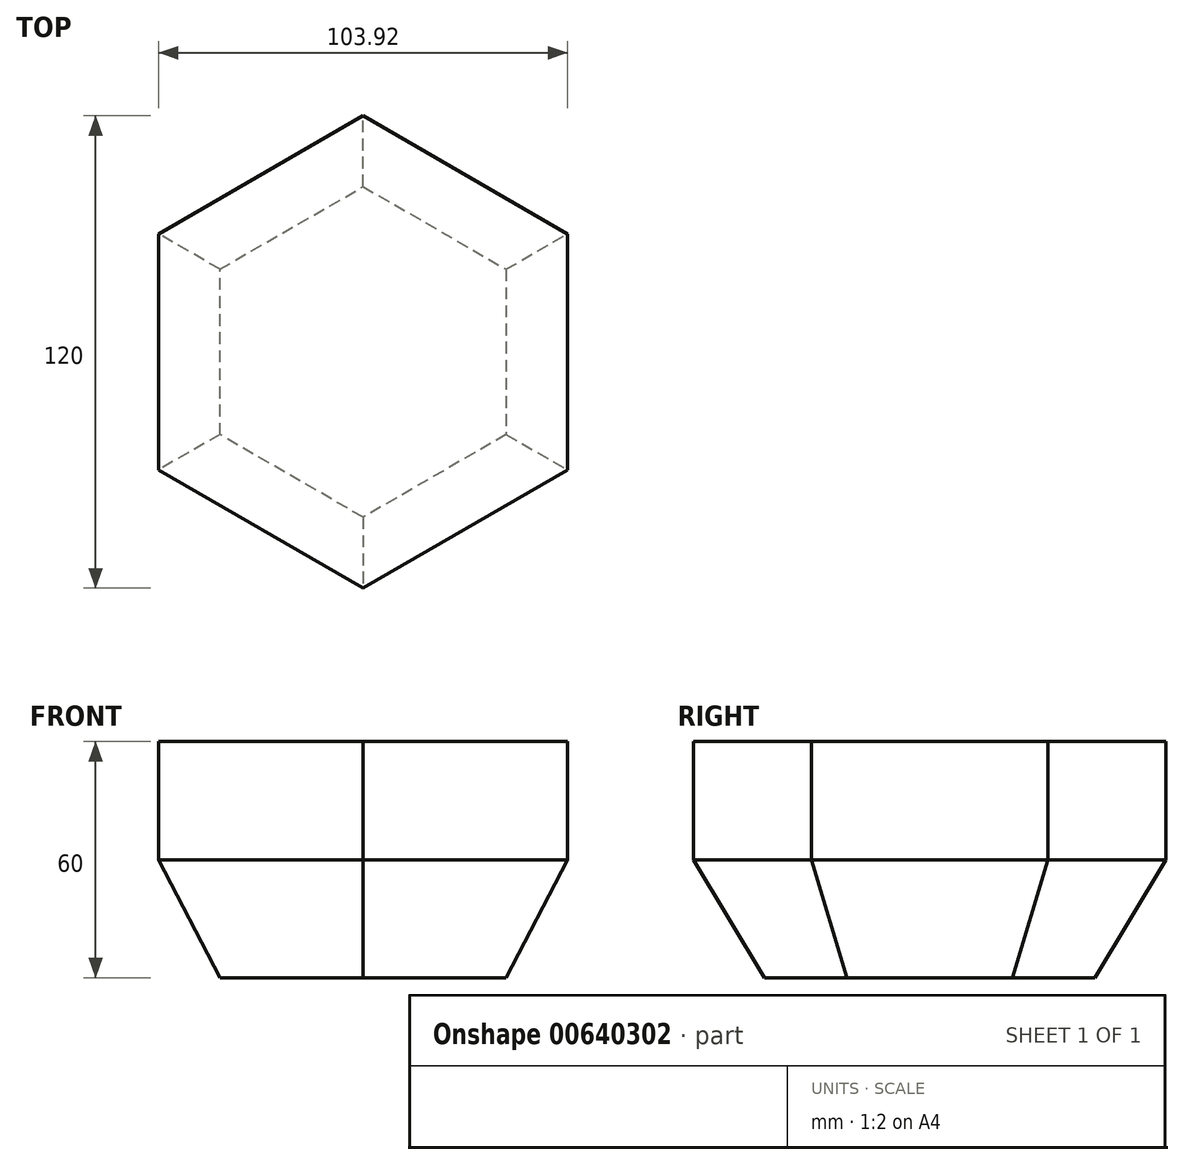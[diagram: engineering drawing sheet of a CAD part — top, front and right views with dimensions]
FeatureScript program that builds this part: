
annotation { "Feature Type Name" : "Feature", "Feature Type Description" : "" }
export const myFeature = defineFeature(function(context is Context, id is Id, definition is map)
    precondition{}
    {
        {
            var Q0;
            Q0=qCreatedBy(makeId("Top.planeOp"),FACE);
            var sketch = newSketch(context, id + "F0", { "sketchPlane" : qUnion([Q0])});
            skCircle(sketch, "E0.cCircle", {"center": v(0, 0) * mm, "radius": 42 * mm, "construction": true});
            skLineSegment(sketch, "E0.0", {"start": v(0, -42) * mm, "end": v(-36.37, -21) * mm});
            skLineSegment(sketch, "E0.1", {"start": v(-36.37, -21) * mm, "end": v(-36.37, 21) * mm});
            skLineSegment(sketch, "E0.2", {"start": v(-36.37, 21) * mm, "end": v(0, 42) * mm});
            skLineSegment(sketch, "E0.3", {"start": v(0, 42) * mm, "end": v(36.37, 21) * mm});
            skLineSegment(sketch, "E0.4", {"start": v(36.37, 21) * mm, "end": v(36.37, -21) * mm});
            skLineSegment(sketch, "E0.5", {"start": v(36.37, -21) * mm, "end": v(0, -42) * mm});
            skSolve(sketch);
        }
        {
            var Q0;
            Q0=makeQuery(id+"F0.imprint","IMPRINT",FACE,{"disambiguationData":[TD([[makeQuery(id+"F0.imprint","IMPRINT",EDGE,{"derivedFrom":sQuery(id+"F0.wireOp",EDGE,"E0.0")}),-1.0]])]});
            cPlane(context, id + "F1", {"entities" : qUnion([Q0]), "cplaneType" : CPlaneType.OFFSET, "offset" : 30 * mm, "width" : 150 * mm, "height" : 150 * mm});
        }
        {
            var Q0;
            Q0=qCreatedBy(id+"F1.planeOp",FACE);
            var sketch = newSketch(context, id + "F2", { "sketchPlane" : qUnion([Q0])});
            skCircle(sketch, "E1.cCircle", {"center": v(0, 0) * mm, "radius": 60 * mm, "construction": true});
            skLineSegment(sketch, "E1.0", {"start": v(0, -60) * mm, "end": v(-51.96, -30) * mm});
            skLineSegment(sketch, "E1.1", {"start": v(-51.96, -30) * mm, "end": v(-51.96, 30) * mm});
            skLineSegment(sketch, "E1.2", {"start": v(-51.96, 30) * mm, "end": v(0, 60) * mm});
            skLineSegment(sketch, "E1.3", {"start": v(0, 60) * mm, "end": v(51.96, 30) * mm});
            skLineSegment(sketch, "E1.4", {"start": v(51.96, 30) * mm, "end": v(51.96, -30) * mm});
            skLineSegment(sketch, "E1.5", {"start": v(51.96, -30) * mm, "end": v(0, -60) * mm});
            skSolve(sketch);
        }
        {
            var Q0;
            Q0=makeQuery(id+"F0.imprint","IMPRINT",FACE,{"disambiguationData":[TD([[makeQuery(id+"F0.imprint","IMPRINT",EDGE,{"derivedFrom":sQuery(id+"F0.wireOp",EDGE,"E0.0")}),-1.0]])]});
            var Q1;
            Q1=makeQuery(id+"F2.imprint","IMPRINT",FACE,{"disambiguationData":[TD([[makeQuery(id+"F2.imprint","IMPRINT",EDGE,{"derivedFrom":sQuery(id+"F2.wireOp",EDGE,"E1.0")}),-1.0]])]});
            loft(context, id + "F3", {"sheetProfilesArray" : [{ "sheetProfileEntities" : qUnion([Q0]) }, { "sheetProfileEntities" : qUnion([Q1]) }]});
        }
        {
            var Q0;
            Q0=makeQuery(id+"F3.opLoft","CAP_FACE",FACE,{"disambiguationData":[OSD([makeQuery(id+"F2.imprint","IMPRINT",FACE,{"disambiguationData":[TD([[makeQuery(id+"F2.imprint","IMPRINT",EDGE,{"derivedFrom":sQuery(id+"F2.wireOp",EDGE,"E1.0")}),-1.0]])]})])],"isStart":true});
            extrude(context, id + "F4", {"entities" : qUnion([Q0]), "operationType" : NewBodyOperationType.ADD, "depth" : 30 * mm, "offsetDistance" : 25 * mm});
        }
    });
